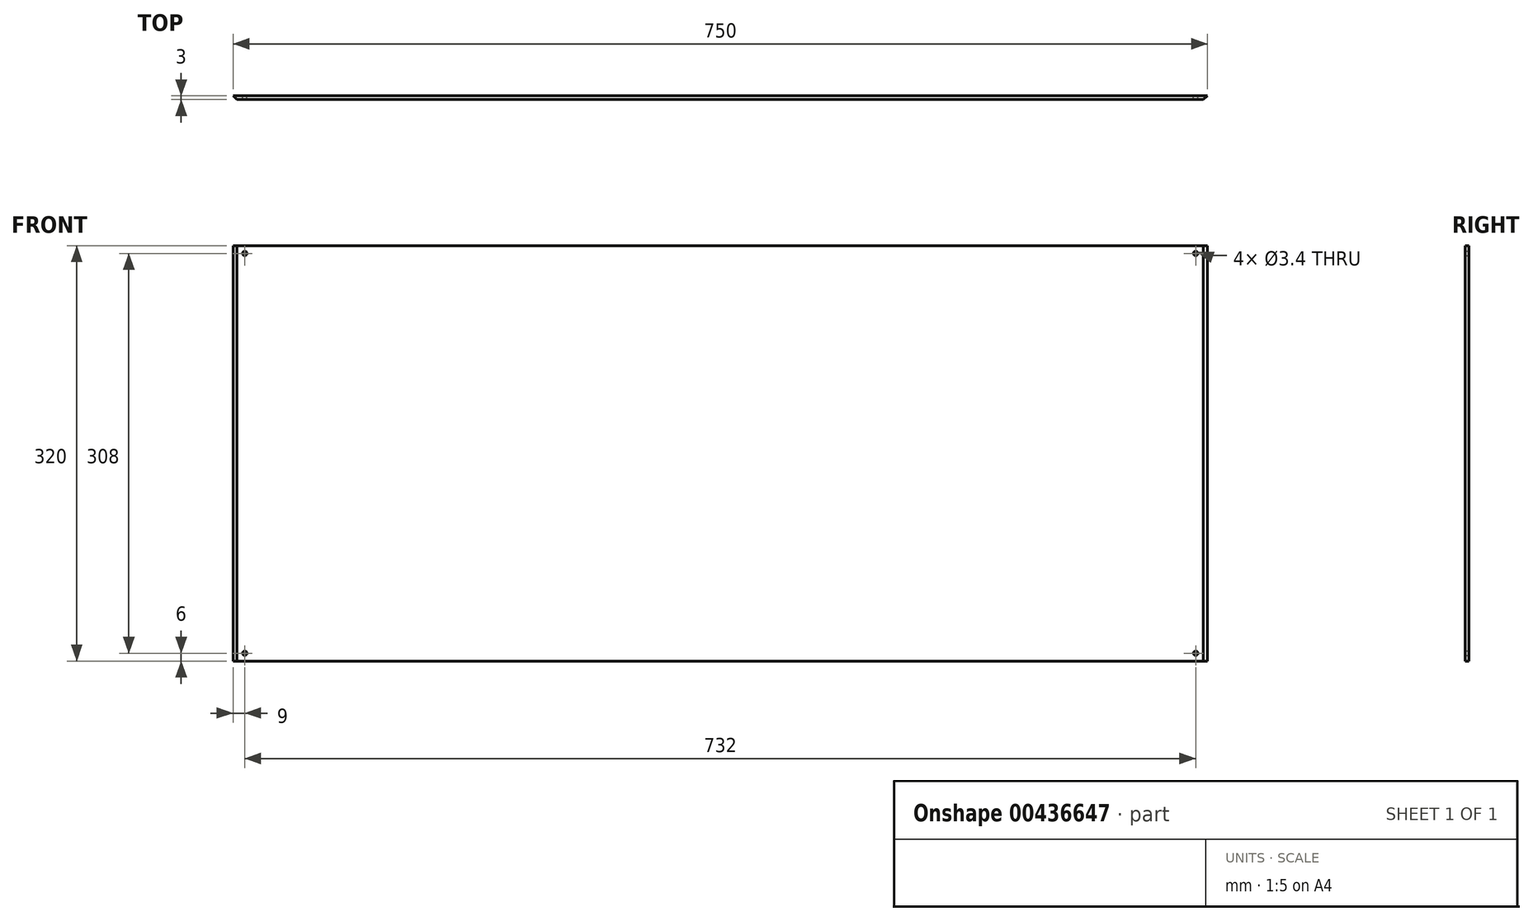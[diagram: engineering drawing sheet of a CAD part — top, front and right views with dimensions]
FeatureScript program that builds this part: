
annotation { "Feature Type Name" : "Feature", "Feature Type Description" : "" }
export const myFeature = defineFeature(function(context is Context, id is Id, definition is map)
    precondition{}
    {
        {
            var Q0;
            Q0=qCreatedBy(makeId("Top.planeOp"),FACE);
            var sketch = newSketch(context, id + "F0", { "sketchPlane" : qUnion([Q0])});
            skLineSegment(sketch, "E0", {"start": v(0, 0) * mm, "end": v(0, 1.5) * mm, "construction": true});
            skLineSegment(sketch, "E1", {"start": v(0, 0) * mm, "end": v(0, -1.5) * mm, "construction": true});
            skLineSegment(sketch, "E2", {"start": v(0, 1.5) * mm, "end": v(-375, 1.5) * mm});
            skLineSegment(sketch, "E3", {"start": v(0, 1.5) * mm, "end": v(375, 1.5) * mm});
            skLineSegment(sketch, "E4", {"start": v(0, -1.5) * mm, "end": v(-372, -1.5) * mm});
            skLineSegment(sketch, "E5", {"start": v(0, -1.5) * mm, "end": v(372, -1.5) * mm});
            skLineSegment(sketch, "E6", {"start": v(-372, -1.5) * mm, "end": v(-375, 1.5) * mm});
            skLineSegment(sketch, "E7", {"start": v(372, -1.5) * mm, "end": v(375, 1.5) * mm});
            skSolve(sketch);
        }
        {
            var Q0;
            Q0=makeQuery(id+"F0.imprint","IMPRINT",FACE,{"disambiguationData":[TD([[makeQuery(id+"F0.imprint","IMPRINT",EDGE,{"derivedFrom":sQuery(id+"F0.wireOp",EDGE,"E2")}),1.0]])]});
            extrude(context, id + "F1", {"entities" : qUnion([Q0]), "depth" : 320 * mm});
        }
        {
            var Q0;
            Q0=makeQuery(id+"F1.opExtrude","SWEPT_FACE",FACE,{"disambiguationData":[OSD([sQuery(id+"F0.wireOp",EDGE,"E2"),sQuery(id+"F0.wireOp",EDGE,"E3")])]});
            var sketch = newSketch(context, id + "F2", { "sketchPlane" : qUnion([Q0])});
            skLineSegment(sketch, "E8", {"start": v(0, 320) * mm, "end": v(-366, 320) * mm, "construction": true});
            skLineSegment(sketch, "E9", {"start": v(-366, 320) * mm, "end": v(-366, 314) * mm, "construction": true});
            skCircle(sketch, "E10", {"center": v(-366, 314) * mm, "radius": 1.7 * mm});
            skLineSegment(sketch, "E11", {"start": v(-366, 314) * mm, "end": v(-366, 6) * mm, "construction": true});
            skCircle(sketch, "E12", {"center": v(-366, 6) * mm, "radius": 1.7 * mm});
            skLineSegment(sketch, "E13", {"start": v(0, 320) * mm, "end": v(366, 320) * mm, "construction": true});
            skLineSegment(sketch, "E14", {"start": v(366, 320) * mm, "end": v(366, 314) * mm, "construction": true});
            skLineSegment(sketch, "E15", {"start": v(366, 314) * mm, "end": v(366, 6) * mm, "construction": true});
            skCircle(sketch, "E16", {"center": v(366, 314) * mm, "radius": 1.7 * mm});
            skCircle(sketch, "E17", {"center": v(366, 6) * mm, "radius": 1.7 * mm});
            skLineSegment(sketch, "E18", {"start": v(0, 0) * mm, "end": v(0, 320) * mm, "construction": true});
            skSolve(sketch);
        }
        {
            var Q0;
            Q0=makeQuery(id+"F2.imprint","IMPRINT",FACE,{"disambiguationData":[TD([[makeQuery(id+"F2.imprint","IMPRINT",EDGE,{"derivedFrom":sQuery(id+"F2.wireOp",EDGE,"E10")}),1.0]])]});
            var Q1;
            Q1=makeQuery(id+"F2.imprint","IMPRINT",FACE,{"disambiguationData":[TD([[makeQuery(id+"F2.imprint","IMPRINT",EDGE,{"derivedFrom":sQuery(id+"F2.wireOp",EDGE,"E16")}),1.0]])]});
            var Q2;
            Q2=makeQuery(id+"F2.imprint","IMPRINT",FACE,{"disambiguationData":[TD([[makeQuery(id+"F2.imprint","IMPRINT",EDGE,{"derivedFrom":sQuery(id+"F2.wireOp",EDGE,"E17")}),1.0]])]});
            var Q3;
            Q3=makeQuery(id+"F2.imprint","IMPRINT",FACE,{"disambiguationData":[TD([[makeQuery(id+"F2.imprint","IMPRINT",EDGE,{"derivedFrom":sQuery(id+"F2.wireOp",EDGE,"E12")}),1.0]])]});
            extrude(context, id + "F3", {"entities" : qUnion([Q0, Q1, Q2, Q3]), "operationType" : NewBodyOperationType.REMOVE, "oppositeDirection" : true, "depth" : 3 * mm});
        }
    });
